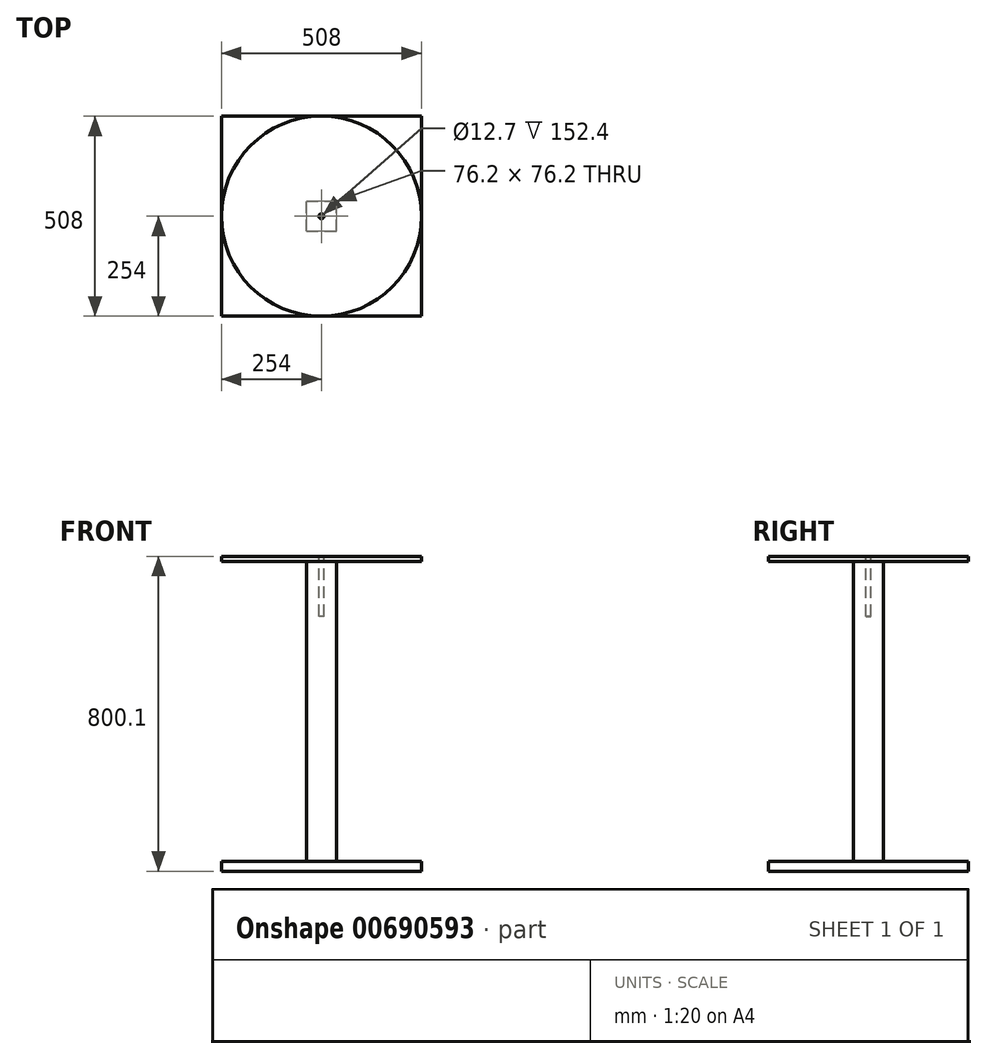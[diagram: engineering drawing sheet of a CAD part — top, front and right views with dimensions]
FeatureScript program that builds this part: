
annotation { "Feature Type Name" : "Feature", "Feature Type Description" : "" }
export const myFeature = defineFeature(function(context is Context, id is Id, definition is map)
    precondition{}
    {
        {
            var Q0;
            Q0=qCreatedBy(makeId("Top.planeOp"),FACE);
            var sketch = newSketch(context, id + "F0", { "sketchPlane" : qUnion([Q0])});
            skLineSegment(sketch, "E0.bottom", {"start": v(-254, -254) * mm, "end": v(254, -254) * mm});
            skLineSegment(sketch, "E0.top", {"start": v(-254, 254) * mm, "end": v(254, 254) * mm});
            skLineSegment(sketch, "E0.left", {"start": v(-254, -254) * mm, "end": v(-254, 254) * mm});
            skLineSegment(sketch, "E0.right", {"start": v(254, -254) * mm, "end": v(254, 254) * mm});
            skSolve(sketch);
        }
        {
            var Q0;
            Q0 = qSketchRegion(id + "F0", true);
            extrude(context, id + "F1", {"entities" : qUnion([Q0]), "depth" : 25.4 * mm, "offsetDistance" : 25.4 * mm});
        }
        {
            var Q0;
            Q0=makeQuery(id+"F1.opExtrude","CAP_FACE",FACE,{"disambiguationData":[OSD([sQuery(id+"F0.wireOp",EDGE,"E0.bottom"),sQuery(id+"F0.wireOp",EDGE,"E0.top"),sQuery(id+"F0.wireOp",EDGE,"E0.left"),sQuery(id+"F0.wireOp",EDGE,"E0.right")])],"isStart":false});
            var sketch = newSketch(context, id + "F2", { "sketchPlane" : qUnion([Q0])});
            skLineSegment(sketch, "E1.bottom", {"start": v(-38.1, -38.1) * mm, "end": v(38.1, -38.1) * mm});
            skLineSegment(sketch, "E1.top", {"start": v(-38.1, 38.1) * mm, "end": v(38.1, 38.1) * mm});
            skLineSegment(sketch, "E1.left", {"start": v(-38.1, -38.1) * mm, "end": v(-38.1, 38.1) * mm});
            skLineSegment(sketch, "E1.right", {"start": v(38.1, -38.1) * mm, "end": v(38.1, 38.1) * mm});
            skSolve(sketch);
        }
        {
            var Q0;
            Q0 = qSketchRegion(id + "F2", true);
            extrude(context, id + "F3", {"entities" : qUnion([Q0]), "operationType" : NewBodyOperationType.ADD, "depth" : 762 * mm, "offsetDistance" : 25.4 * mm});
        }
        {
            var Q0;
            Q0=makeQuery(id+"F3.opExtrude","CAP_FACE",FACE,{"disambiguationData":[OSD([sQuery(id+"F2.wireOp",EDGE,"E1.bottom"),sQuery(id+"F2.wireOp",EDGE,"E1.top"),sQuery(id+"F2.wireOp",EDGE,"E1.left"),sQuery(id+"F2.wireOp",EDGE,"E1.right")])],"isStart":false});
            var sketch = newSketch(context, id + "F4", { "sketchPlane" : qUnion([Q0])});
            skCircle(sketch, "E2", {"center": v(0, 0) * mm, "radius": 254 * mm});
            skSolve(sketch);
        }
        {
            var Q0;
            Q0 = qSketchRegion(id + "F4", true);
            extrude(context, id + "F5", {"entities" : qUnion([Q0]), "operationType" : NewBodyOperationType.ADD, "depth" : 12.7 * mm, "offsetDistance" : 25.4 * mm});
        }
        {
            var Q0;
            Q0=makeQuery(id+"F5.opExtrude","CAP_FACE",FACE,{"disambiguationData":[OSD([sQuery(id+"F4.wireOp",EDGE,"E2")])],"isStart":false});
            var sketch = newSketch(context, id + "F6", { "sketchPlane" : qUnion([Q0])});
            skCircle(sketch, "E3", {"center": v(0, 0) * mm, "radius": 6.35 * mm});
            skSolve(sketch);
        }
        {
            var Q0;
            Q0 = qSketchRegion(id + "F6", true);
            extrude(context, id + "F7", {"entities" : qUnion([Q0]), "operationType" : NewBodyOperationType.REMOVE, "oppositeDirection" : true, "depth" : 152.4 * mm, "offsetDistance" : 25.4 * mm});
        }
    });
